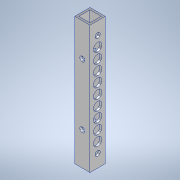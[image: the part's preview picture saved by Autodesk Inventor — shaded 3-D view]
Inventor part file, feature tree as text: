
AUTODESK INVENTOR PART (.ipt)
format: ipt  version: 2020.3 (Build 243373000, 373)  size: 177,152 bytes
history: native  units: mm
features: sketch x4, hole x3, other x1, extrude x1
ambient origin geometry x8: Origin, YZ Plane, XZ Plane, XY Plane, X Axis, Y Axis, Z Axis, Center Point
bodies: Body1 (feature_tree)
feature tree (9):
  other  "ソリッド1"
  extrude  "押し出し1"  Depth=9.0mm
  hole  "穴1"  [1 undecoded]
  hole  "穴2"  [1 undecoded]
  hole  "穴3"  [1 undecoded]
  sketch  "スケッチ1"
  sketch  "スケッチ2"
  sketch  "スケッチ3"
  sketch  "スケッチ4"
note: 3 required parameter values undecoded (feature->parameter linkage not recoverable at this tier; creation-order binding heuristic only, values carry confidence <= 0.55)
